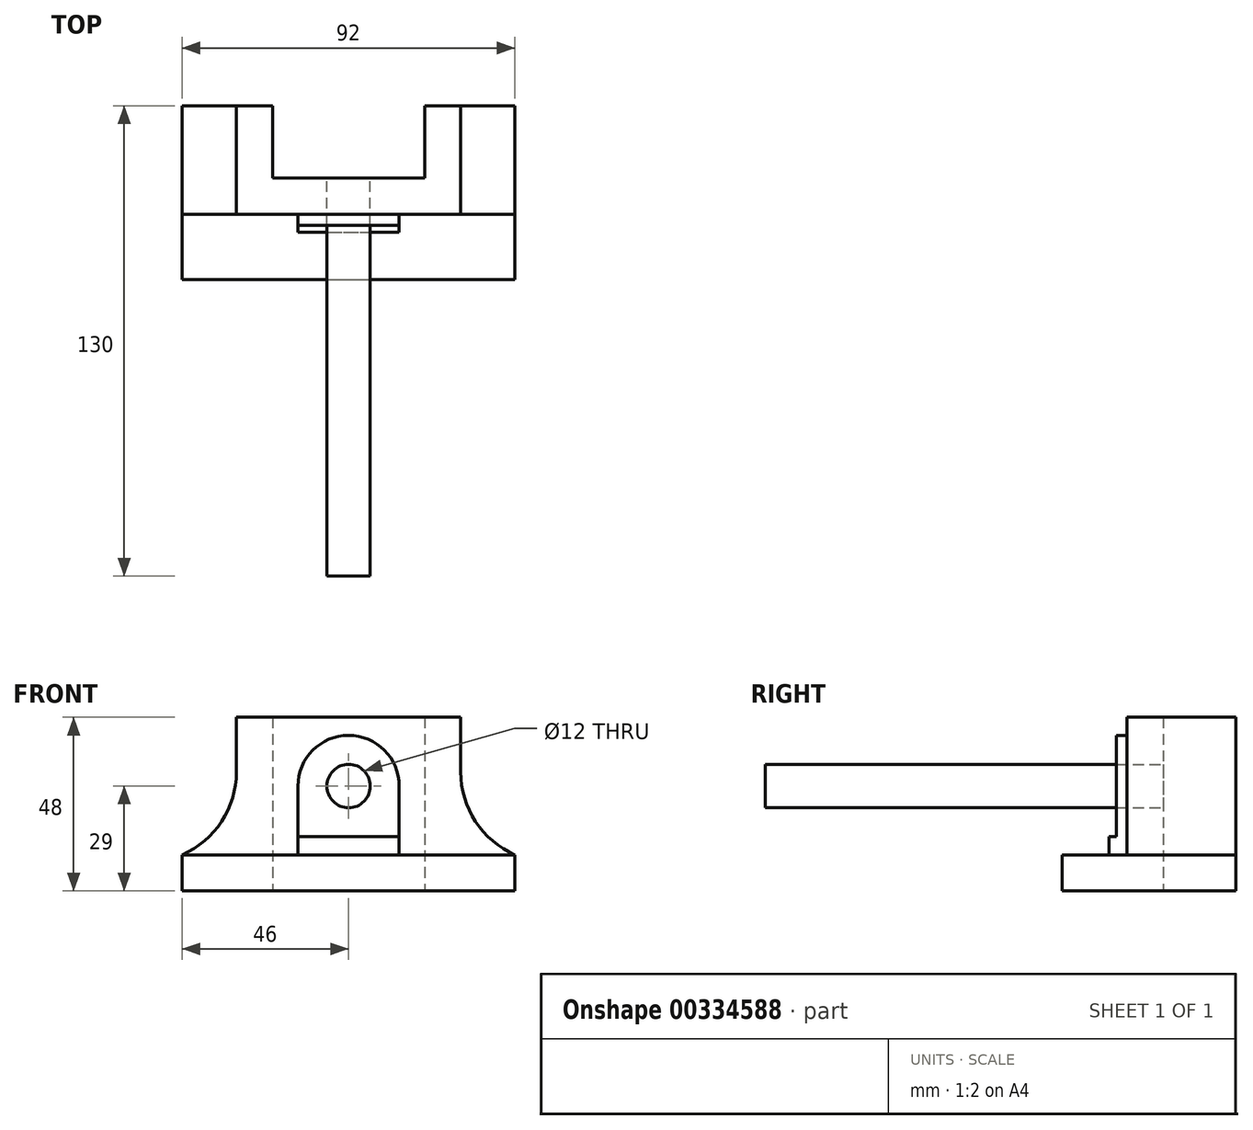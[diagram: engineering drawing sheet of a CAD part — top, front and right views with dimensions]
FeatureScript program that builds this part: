
annotation { "Feature Type Name" : "Feature", "Feature Type Description" : "" }
export const myFeature = defineFeature(function(context is Context, id is Id, definition is map)
    precondition{}
    {
        {
            var Q0;
            Q0=qCreatedBy(makeId("Top.planeOp"),FACE);
            var sketch = newSketch(context, id + "F0", { "sketchPlane" : qUnion([Q0])});
            skLineSegment(sketch, "E0.bottom", {"start": v(-46, -18) * mm, "end": v(46, -18) * mm});
            skLineSegment(sketch, "E0.top", {"start": v(-46, 30) * mm, "end": v(46, 30) * mm});
            skLineSegment(sketch, "E0.left", {"start": v(-46, -18) * mm, "end": v(-46, 30) * mm});
            skLineSegment(sketch, "E0.right", {"start": v(46, -18) * mm, "end": v(46, 30) * mm});
            skLineSegment(sketch, "E1.bottom", {"start": v(-21, 62.23) * mm, "end": v(21, 62.23) * mm});
            skLineSegment(sketch, "E1.top", {"start": v(-21, 10) * mm, "end": v(21, 10) * mm});
            skLineSegment(sketch, "E1.left", {"start": v(-21, 62.23) * mm, "end": v(-21, 10) * mm});
            skLineSegment(sketch, "E1.right", {"start": v(21, 62.23) * mm, "end": v(21, 10) * mm});
            skLineSegment(sketch, "E2", {"start": v(-46, 0) * mm, "end": v(46, 0) * mm});
            skSolve(sketch);
        }
        {
            var Q0;
            {var subQ10=sQuery(id+"F0.wireOp",EDGE,"E1.top");Q0=makeQuery(id+"F0.imprint","IMPRINT",FACE,{"disambiguationData":[TD([[makeQuery(id+"F0.imprint","IMPRINT",EDGE,{"derivedFrom":subQ10}),-1.0]])]});}
            extrude(context, id + "F1", {"entities" : qUnion([Q0]), "depth" : 48 * mm});
        }
        {
            var Q0;
            {var subQ0=sQuery(id+"F0.wireOp",EDGE,"E0.bottom");Q0=makeQuery(id+"F0.imprint","IMPRINT",FACE,{"disambiguationData":[TD([[makeQuery(id+"F0.imprint","IMPRINT",EDGE,{"derivedFrom":subQ0}),1.0]])]});}
            extrude(context, id + "F2", {"entities" : qUnion([Q0]), "operationType" : NewBodyOperationType.ADD, "depth" : 10 * mm});
        }
        {
            var Q0;
            Q0=makeQuery(id+"F1.opExtrude","SWEPT_FACE",FACE,{"disambiguationData":[OSD([sQuery(id+"F0.wireOp",EDGE,"E2")])]});
            var sketch = newSketch(context, id + "F3", { "sketchPlane" : qUnion([Q0])});
            skLineSegment(sketch, "E3", {"start": v(-31, 58.46) * mm, "end": v(-31, 10) * mm});
            skLineSegment(sketch, "E4", {"start": v(31, 58.85) * mm, "end": v(31, 10) * mm});
            skLineSegment(sketch, "E5", {"start": v(-31, 58.46) * mm, "end": v(-68.46, 62.74) * mm});
            skLineSegment(sketch, "E6", {"start": v(-68.46, 62.74) * mm, "end": v(-62.94, 10) * mm});
            skLineSegment(sketch, "E7", {"start": v(-62.94, 10) * mm, "end": v(-31, 10) * mm});
            skLineSegment(sketch, "E8", {"start": v(31, 58.85) * mm, "end": v(62.62, 62.42) * mm});
            skLineSegment(sketch, "E9", {"start": v(62.62, 62.42) * mm, "end": v(62.62, 10) * mm});
            skLineSegment(sketch, "E10", {"start": v(62.62, 10) * mm, "end": v(31, 10) * mm});
            skSolve(sketch);
        }
        {
            var Q0;
            {var subQ4=sQuery(id+"F3.wireOp",EDGE,"E5");Q0=makeQuery(id+"F3.imprint","IMPRINT",FACE,{"disambiguationData":[TD([[makeQuery(id+"F3.imprint","IMPRINT",EDGE,{"derivedFrom":subQ4}),1.0]])]});}
            var Q1;
            {var subQ4=sQuery(id+"F3.wireOp",EDGE,"E8");Q1=makeQuery(id+"F3.imprint","IMPRINT",FACE,{"disambiguationData":[TD([[makeQuery(id+"F3.imprint","IMPRINT",EDGE,{"derivedFrom":subQ4}),-1.0]])]});}
            var Q2;
            {var subQ2=sQuery(id+"F0.wireOp",EDGE,"E2");var subQ6=makeQuery(id+"F1.opExtrude","SWEPT_EDGE",EDGE,{"disambiguationData":[OSD([sQuery(id+"F0.wireOp",EDGE,"E0.left"),subQ2])]});Q2=makeQuery(id+"F3.imprint","IMPRINT",FACE,{"disambiguationData":[TD([[makeQuery(id+"F3.imprint","IMPRINT",EDGE,{"derivedFrom":subQ6}),1.0]])]});}
            var Q3;
            {var subQ2=sQuery(id+"F0.wireOp",EDGE,"E2");var subQ6=makeQuery(id+"F1.opExtrude","SWEPT_EDGE",EDGE,{"disambiguationData":[OSD([sQuery(id+"F0.wireOp",EDGE,"E0.right"),subQ2])]});Q3=makeQuery(id+"F3.imprint","IMPRINT",FACE,{"disambiguationData":[TD([[makeQuery(id+"F3.imprint","IMPRINT",EDGE,{"derivedFrom":subQ6}),-1.0]])]});}
            extrude(context, id + "F4", {"entities" : qUnion([Q0, Q1, Q2, Q3]), "operationType" : NewBodyOperationType.REMOVE, "oppositeDirection" : true, "depth" : 50 * mm});
        }
        {
            var Q0;
            Q0=makeQuery(id+"F4.boolean.opBoolean","COPY",EDGE,{"derivedFrom":makeQuery(id+"F4.opExtrude","SWEPT_EDGE",EDGE,{"disambiguationData":[OSD([sQuery(id+"F0.wireOp",EDGE,"E2"),sQuery(id+"F3.wireOp",EDGE,"E3"),sQuery(id+"F3.wireOp",EDGE,"E7")])]})});
            var Q1;
            Q1=makeQuery(id+"F4.boolean.opBoolean","COPY",EDGE,{"derivedFrom":makeQuery(id+"F4.opExtrude","SWEPT_EDGE",EDGE,{"disambiguationData":[OSD([sQuery(id+"F0.wireOp",EDGE,"E2"),sQuery(id+"F3.wireOp",EDGE,"E4"),sQuery(id+"F3.wireOp",EDGE,"E10")])]})});
            fillet(context, id + "F5", {"entities" : qUnion([Q0, Q1]), "radius" : 25 * mm, "tangentPropagation" : true, "allowEdgeOverflow" : false});
        }
        {
            var Q0;
            Q0=makeQuery(id+"F1.opExtrude","SWEPT_FACE",FACE,{"disambiguationData":[OSD([sQuery(id+"F0.wireOp",EDGE,"E2")])]});
            var sketch = newSketch(context, id + "F6", { "sketchPlane" : qUnion([Q0])});
            skCircle(sketch, "E11", {"center": v(0, 29) * mm, "radius": 14 * mm});
            skLineSegment(sketch, "E12", {"start": v(-14, 29) * mm, "end": v(-14, 10) * mm});
            skLineSegment(sketch, "E13", {"start": v(14, 29) * mm, "end": v(14, 10) * mm});
            skLineSegment(sketch, "E14", {"start": v(14, 10) * mm, "end": v(-14, 10) * mm});
            skLineSegment(sketch, "E15", {"start": v(-14, 15) * mm, "end": v(14, 15) * mm});
            skCircle(sketch, "E16", {"center": v(0, 29) * mm, "radius": 6 * mm});
            skSolve(sketch);
        }
        {
            var Q0;
            Q0=makeQuery(id+"F6.imprint","IMPRINT",FACE,{"disambiguationData":[TD([[makeQuery(id+"F6.imprint","IMPRINT",EDGE,{"derivedFrom":sQuery(id+"F6.wireOp",EDGE,"E16")}),-1.0]])]});
            var Q1;
            {var subQ0=sQuery(id+"F6.wireOp",EDGE,"E12");var subQ1=sQuery(id+"F6.wireOp",EDGE,"E11");var subQ2=makeQuery(id+"F6.imprint","INTERSECT",VERTEX,{"derivedFrom":[subQ1,subQ0]});Q1=makeQuery(id+"F6.imprint","IMPRINT",FACE,{"disambiguationData":[TD([[makeQuery(id+"F6.imprint","IMPRINT",EDGE,{"disambiguationData":[TD([[subQ2,-1.0]])],"derivedFrom":subQ1}),-1.0]])]});}
            var Q2;
            {var subQ0=sQuery(id+"F6.wireOp",EDGE,"E13");var subQ1=sQuery(id+"F6.wireOp",EDGE,"E11");var subQ2=makeQuery(id+"F6.imprint","INTERSECT",VERTEX,{"derivedFrom":[subQ1,subQ0]});Q2=makeQuery(id+"F6.imprint","IMPRINT",FACE,{"disambiguationData":[TD([[makeQuery(id+"F6.imprint","IMPRINT",EDGE,{"disambiguationData":[TD([[subQ2,1.0]])],"derivedFrom":subQ1}),-1.0]])]});}
            extrude(context, id + "F7", {"entities" : qUnion([Q0, Q1, Q2]), "operationType" : NewBodyOperationType.ADD, "depth" : 3 * mm});
        }
        {
            var Q0;
            {var subQ4=sQuery(id+"F6.wireOp",EDGE,"E14");Q0=makeQuery(id+"F6.imprint","IMPRINT",FACE,{"disambiguationData":[TD([[makeQuery(id+"F6.imprint","IMPRINT",EDGE,{"derivedFrom":subQ4}),1.0]])]});}
            extrude(context, id + "F8", {"entities" : qUnion([Q0]), "operationType" : NewBodyOperationType.ADD, "depth" : 5 * mm});
        }
        {
            var Q0;
            Q0=makeQuery(id+"F6.imprint","IMPRINT",FACE,{"disambiguationData":[TD([[makeQuery(id+"F6.imprint","IMPRINT",EDGE,{"derivedFrom":sQuery(id+"F6.wireOp",EDGE,"E16")}),1.0]])]});
            extrude(context, id + "F9", {"entities" : qUnion([Q0]), "operationType" : NewBodyOperationType.REMOVE, "oppositeDirection" : true, "depth" : 25 * mm});
        }
        {
            var Q0;
            Q0=makeQuery(id+"F6.imprint","IMPRINT",FACE,{"disambiguationData":[TD([[makeQuery(id+"F6.imprint","IMPRINT",EDGE,{"derivedFrom":sQuery(id+"F6.wireOp",EDGE,"E16")}),1.0]])]});
            var Q1;
            Q1=sQuery(id+"F6.wireOp",EDGE,"E16");
            extrude(context, id + "F10", {"entities" : qUnion([Q0]), "surfaceEntities" : qUnion([Q1]), "depth" : 100 * mm});
        }
    });
